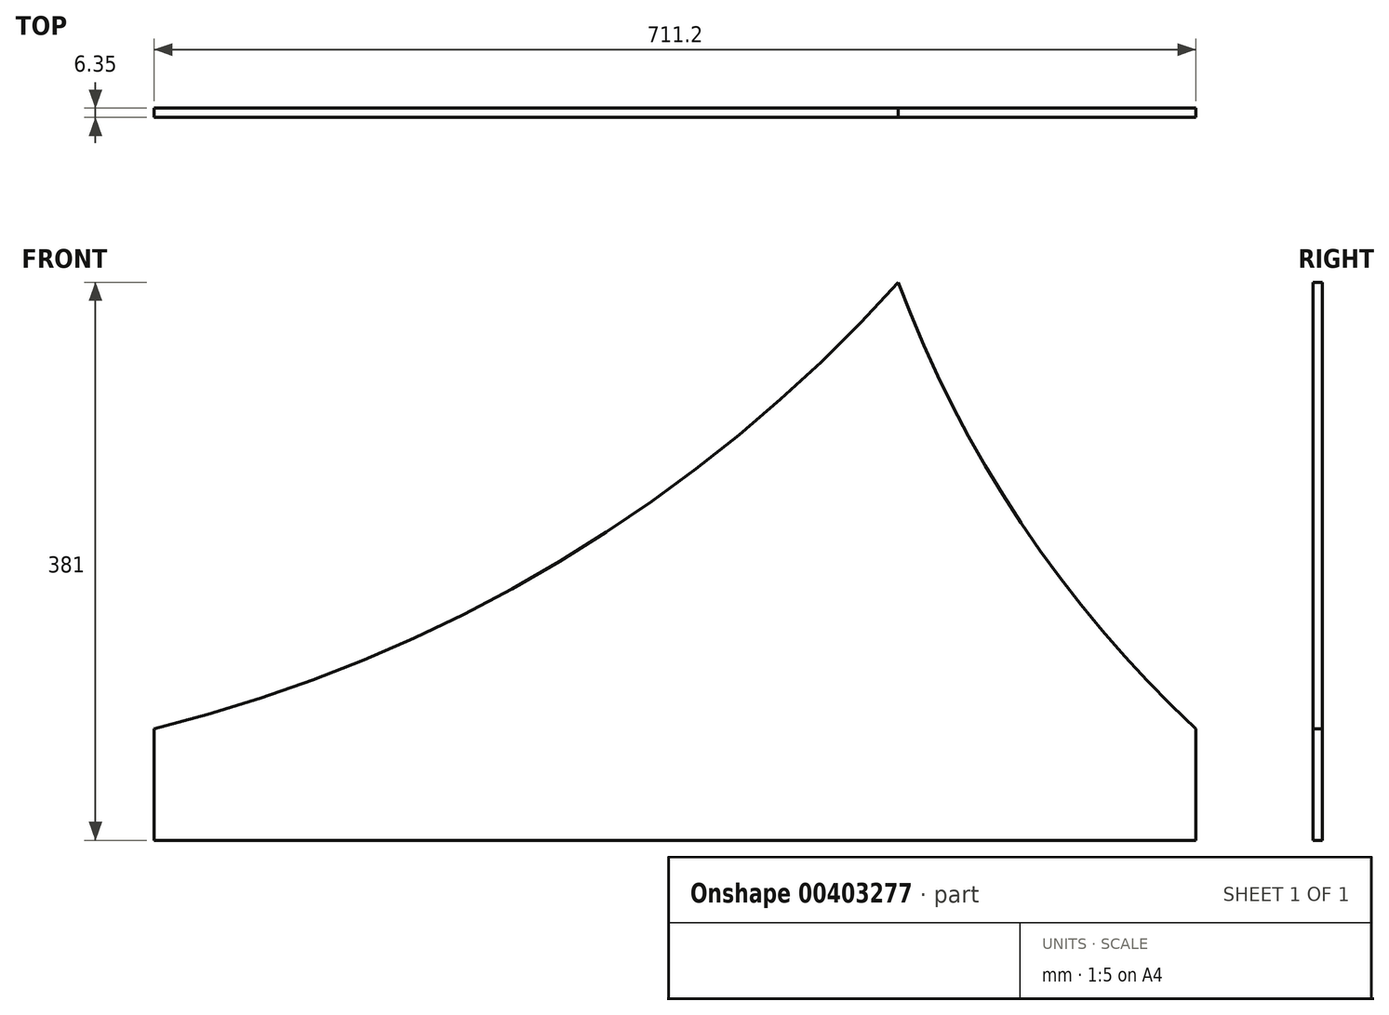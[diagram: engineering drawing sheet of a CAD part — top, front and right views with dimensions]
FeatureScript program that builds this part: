
annotation { "Feature Type Name" : "Feature", "Feature Type Description" : "" }
export const myFeature = defineFeature(function(context is Context, id is Id, definition is map)
    precondition{}
    {
        {
            var Q0;
            Q0=qCreatedBy(makeId("Front.planeOp"),FACE);
            var sketch = newSketch(context, id + "F0", { "sketchPlane" : qUnion([Q0])});
            skLineSegment(sketch, "E0", {"start": v(0, 0) * mm, "end": v(711.2, 0) * mm});
            skLineSegment(sketch, "E1.bottom", {"start": v(0, 0) * mm, "end": v(431.8, 0) * mm});
            skLineSegment(sketch, "E1.top", {"start": v(0, 228.6) * mm, "end": v(431.8, 228.6) * mm});
            skLineSegment(sketch, "E1.left", {"start": v(0, 0) * mm, "end": v(0, 228.6) * mm});
            skLineSegment(sketch, "E1.right", {"start": v(431.8, 0) * mm, "end": v(431.8, 228.6) * mm});
            skLineSegment(sketch, "E2.bottom", {"start": v(0, 0) * mm, "end": v(508, 0) * mm});
            skLineSegment(sketch, "E2.top", {"start": v(0, 304.8) * mm, "end": v(508, 304.8) * mm});
            skLineSegment(sketch, "E2.left", {"start": v(0, 0) * mm, "end": v(0, 304.8) * mm});
            skLineSegment(sketch, "E2.right", {"start": v(508, 0) * mm, "end": v(508, 304.8) * mm});
            skLineSegment(sketch, "E3.bottom", {"start": v(0, 0) * mm, "end": v(584.2, 0) * mm});
            skLineSegment(sketch, "E3.top", {"start": v(0, 152.4) * mm, "end": v(584.2, 152.4) * mm});
            skLineSegment(sketch, "E3.left", {"start": v(0, 0) * mm, "end": v(0, 152.4) * mm});
            skLineSegment(sketch, "E3.right", {"start": v(584.2, 0) * mm, "end": v(584.2, 152.4) * mm});
            skLineSegment(sketch, "E4.top", {"start": v(0, -76.2) * mm, "end": v(711.2, -76.2) * mm});
            skLineSegment(sketch, "E4.left", {"start": v(0, 0) * mm, "end": v(0, -76.2) * mm});
            skLineSegment(sketch, "E4.right", {"start": v(711.2, 0) * mm, "end": v(711.2, -76.2) * mm});
            skCircle(sketch, "E5", {"center": v(-241.3, 977.9) * mm, "radius": 1007.23 * mm});
            skCircle(sketch, "E6", {"center": v(1257.3, 584.2) * mm, "radius": 799.7 * mm});
            skSolve(sketch);
        }
        {
            var Q0;
            {var subQ1=sQuery(id+"F0.wireOp",EDGE,"E1.right");var subQ3=sQuery(id+"F0.wireOp",EDGE,"E3.top");var subQ4=makeQuery(id+"F0.imprint","INTERSECT",VERTEX,{"derivedFrom":[subQ1,subQ3]});Q0=makeQuery(id+"F0.imprint","IMPRINT",FACE,{"disambiguationData":[TD([[makeQuery(id+"F0.imprint","IMPRINT",EDGE,{"disambiguationData":[TD([[subQ4,1.0]])],"derivedFrom":subQ3}),1.0]])]});}
            var Q1;
            {var subQ0=sQuery(id+"F0.wireOp",EDGE,"E0");var subQ1=sQuery(id+"F0.wireOp",EDGE,"E1.right");var subQ2=makeQuery(id+"F0.imprint","INTERSECT",VERTEX,{"derivedFrom":[subQ1,subQ0]});Q1=makeQuery(id+"F0.imprint","IMPRINT",FACE,{"disambiguationData":[TD([[makeQuery(id+"F0.imprint","IMPRINT",EDGE,{"disambiguationData":[TD([[subQ2,-1.0]])],"derivedFrom":subQ1}),1.0]])]});}
            var Q2;
            {var subQ1=sQuery(id+"F0.wireOp",EDGE,"E1.right");var subQ3=sQuery(id+"F0.wireOp",EDGE,"E3.top");var subQ4=makeQuery(id+"F0.imprint","INTERSECT",VERTEX,{"derivedFrom":[subQ1,subQ3]});Q2=makeQuery(id+"F0.imprint","IMPRINT",FACE,{"disambiguationData":[TD([[makeQuery(id+"F0.imprint","IMPRINT",EDGE,{"disambiguationData":[TD([[subQ4,-1.0]])],"derivedFrom":subQ3}),1.0]])]});}
            var Q3;
            {var subQ1=sQuery(id+"F0.wireOp",EDGE,"E2.right");var subQ3=sQuery(id+"F0.wireOp",EDGE,"E3.top");var subQ4=makeQuery(id+"F0.imprint","INTERSECT",VERTEX,{"derivedFrom":[subQ1,subQ3]});Q3=makeQuery(id+"F0.imprint","IMPRINT",FACE,{"disambiguationData":[TD([[makeQuery(id+"F0.imprint","IMPRINT",EDGE,{"disambiguationData":[TD([[subQ4,-1.0]])],"derivedFrom":subQ3}),1.0]])]});}
            var Q4;
            {var subQ5=sQuery(id+"F0.wireOp",EDGE,"E3.right");Q4=makeQuery(id+"F0.imprint","IMPRINT",FACE,{"disambiguationData":[TD([[makeQuery(id+"F0.imprint","IMPRINT",EDGE,{"derivedFrom":subQ5}),1.0]])]});}
            var Q5;
            {var subQ0=sQuery(id+"F0.wireOp",EDGE,"E0");var subQ1=sQuery(id+"F0.wireOp",EDGE,"E1.right");var subQ2=makeQuery(id+"F0.imprint","INTERSECT",VERTEX,{"derivedFrom":[subQ1,subQ0]});Q5=makeQuery(id+"F0.imprint","IMPRINT",FACE,{"disambiguationData":[TD([[makeQuery(id+"F0.imprint","IMPRINT",EDGE,{"disambiguationData":[TD([[subQ2,-1.0]])],"derivedFrom":subQ1}),-1.0]])]});}
            var Q6;
            {var subQ0=sQuery(id+"F0.wireOp",EDGE,"E3.right");Q6=makeQuery(id+"F0.imprint","IMPRINT",FACE,{"disambiguationData":[TD([[makeQuery(id+"F0.imprint","IMPRINT",EDGE,{"derivedFrom":subQ0}),-1.0]])]});}
            var Q7;
            Q7=makeQuery(id+"F0.imprint","IMPRINT",FACE,{"disambiguationData":[TD([[makeQuery(id+"F0.imprint","IMPRINT",EDGE,{"derivedFrom":sQuery(id+"F0.wireOp",EDGE,"E4.top")}),1.0]])]});
            extrude(context, id + "F1", {"entities" : qUnion([Q0, Q1, Q2, Q3, Q4, Q5, Q6, Q7]), "depth" : 6.35 * mm});
        }
    });
